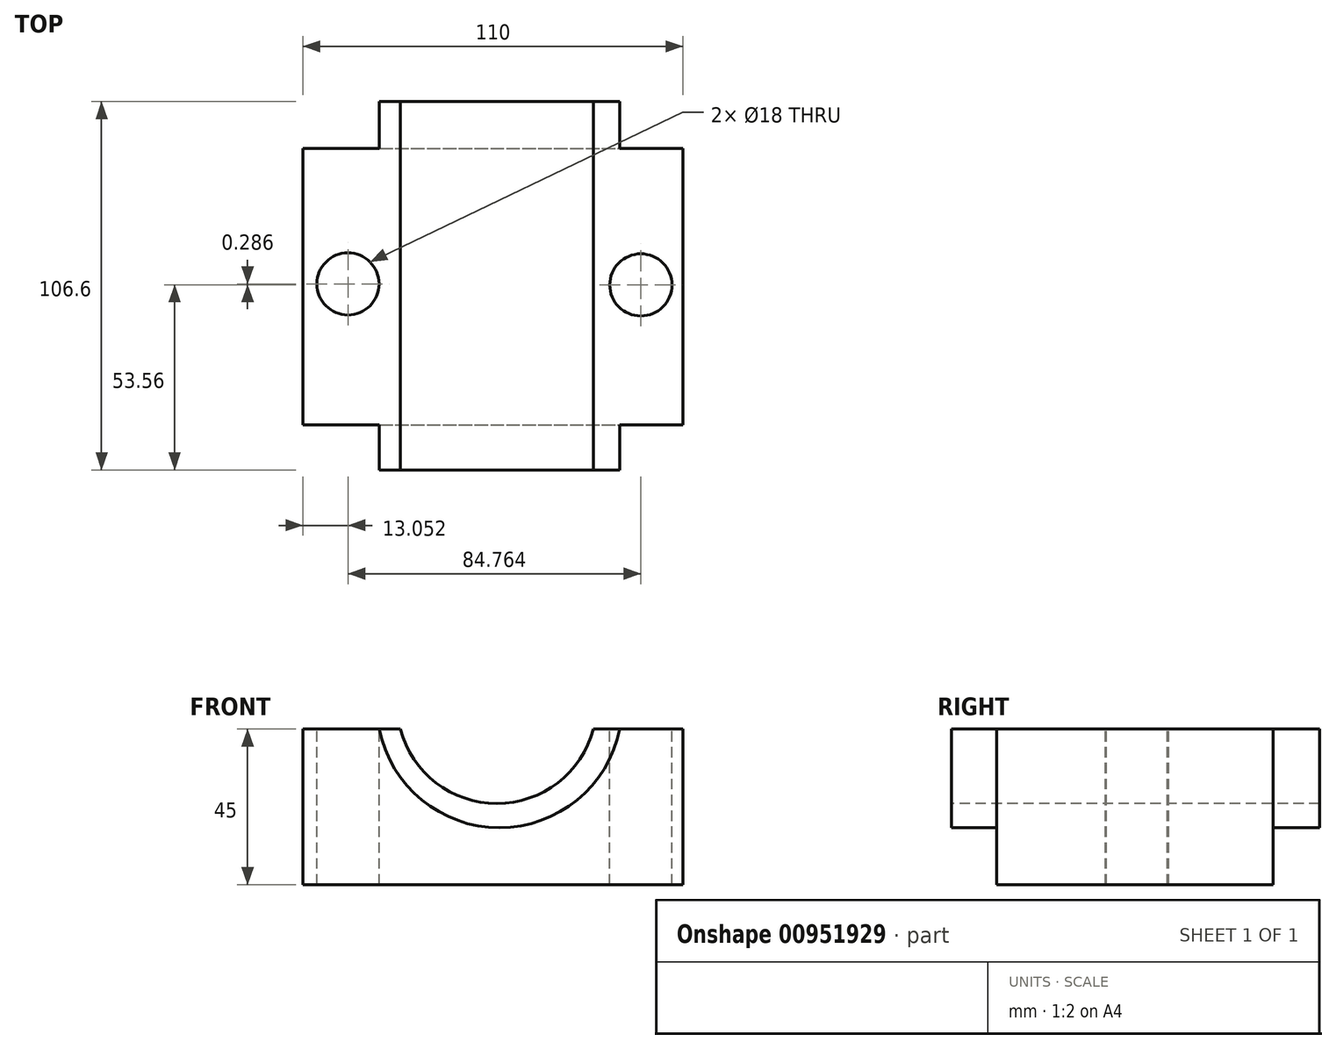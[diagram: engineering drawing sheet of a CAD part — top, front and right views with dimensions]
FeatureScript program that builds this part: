
annotation { "Feature Type Name" : "Feature", "Feature Type Description" : "" }
export const myFeature = defineFeature(function(context is Context, id is Id, definition is map)
    precondition{}
    {
        {
            var Q0;
            Q0=qCreatedBy(makeId("Top.planeOp"),FACE);
            var sketch = newSketch(context, id + "F0", { "sketchPlane" : qUnion([Q0])});
            skLineSegment(sketch, "E0.bottom", {"start": v(-46.7, 32.81) * mm, "end": v(63.3, 32.81) * mm});
            skLineSegment(sketch, "E0.top", {"start": v(-46.7, -47.19) * mm, "end": v(63.3, -47.19) * mm});
            skLineSegment(sketch, "E0.left", {"start": v(-46.7, 32.81) * mm, "end": v(-46.7, -47.19) * mm});
            skLineSegment(sketch, "E0.right", {"start": v(63.3, 32.81) * mm, "end": v(63.3, -47.19) * mm});
            skSolve(sketch);
        }
        {
            var Q0;
            Q0=makeQuery(id+"F0.imprint","IMPRINT",FACE,{"disambiguationData":[TD([[makeQuery(id+"F0.imprint","IMPRINT",EDGE,{"derivedFrom":sQuery(id+"F0.wireOp",EDGE,"E0.bottom")}),-1.0]])]});
            extrude(context, id + "F1", {"entities" : qUnion([Q0]), "oppositeDirection" : true, "depth" : 45 * mm, "offsetDistance" : 25 * mm});
        }
        {
            var Q0;
            Q0=makeQuery(id+"F1.opExtrude","SWEPT_FACE",FACE,{"disambiguationData":[OSD([sQuery(id+"F0.wireOp",EDGE,"E0.top")])]});
            var sketch = newSketch(context, id + "F2", { "sketchPlane" : qUnion([Q0])});
            skArc(sketch, "E1", {"start": v(-18.47, 0) * mm, "mid": v(9.45, -21.54) * mm, "end": v(37.37, 0) * mm});
            skSolve(sketch);
        }
        {
            var Q0;
            {var subQ0=sQuery(id+"F2.wireOp",EDGE,"E1");Q0=makeQuery(id+"F2.imprint","IMPRINT",FACE,{"disambiguationData":[TD([[makeQuery(id+"F2.imprint","IMPRINT",EDGE,{"derivedFrom":subQ0}),1.0]])]});}
            extrude(context, id + "F3", {"entities" : qUnion([Q0]), "operationType" : NewBodyOperationType.REMOVE, "oppositeDirection" : true, "depth" : 136.2 * mm, "offsetDistance" : 25 * mm});
        }
        {
            var Q0;
            Q0=makeQuery(id+"F1.opExtrude","SWEPT_FACE",FACE,{"disambiguationData":[OSD([sQuery(id+"F0.wireOp",EDGE,"E0.top")])]});
            var sketch = newSketch(context, id + "F4", { "sketchPlane" : qUnion([Q0])});
            skArc(sketch, "E2", {"start": v(-24.6, 0) * mm, "mid": v(10.2, -28.55) * mm, "end": v(45, 0) * mm});
            skSolve(sketch);
        }
        {
            var Q0;
            {var subQ0=sQuery(id+"F4.wireOp",EDGE,"E2");Q0=makeQuery(id+"F4.imprint","IMPRINT",FACE,{"disambiguationData":[TD([[makeQuery(id+"F4.imprint","IMPRINT",EDGE,{"derivedFrom":subQ0}),1.0]])]});}
            extrude(context, id + "F5", {"entities" : qUnion([Q0]), "operationType" : NewBodyOperationType.ADD, "oppositeDirection" : true, "depth" : 187 * mm, "offsetDistance" : 25 * mm, "symmetric" : true});
        }
        {
            var Q0;
            Q0=makeQuery(id+"F5.opExtrude","CAP_FACE",FACE,{"disambiguationData":[OSD([sQuery(id+"F0.wireOp",EDGE,"E0.top"),sQuery(id+"F2.wireOp",EDGE,"E1"),sQuery(id+"F4.wireOp",EDGE,"E2")])],"isStart":true});
            extrude(context, id + "F6", {"entities" : qUnion([Q0]), "operationType" : NewBodyOperationType.REMOVE, "oppositeDirection" : true, "depth" : 80.4 * mm, "offsetDistance" : 25 * mm});
        }
        {
            var Q0;
            {var subQ0=sQuery(id+"F0.wireOp",EDGE,"E0.left");var subQ1=sQuery(id+"F0.wireOp",EDGE,"E0.top");var subQ2=sQuery(id+"F0.wireOp",EDGE,"E0.bottom");var subQ3=makeQuery(id+"F1.opExtrude","CAP_FACE",FACE,{"disambiguationData":[OSD([subQ2,subQ1,subQ0,sQuery(id+"F0.wireOp",EDGE,"E0.right")])],"isStart":true});var subQ5=sQuery(id+"F2.wireOp",EDGE,"E1");var subQ7=makeQuery(id+"F1.opExtrude","SWEPT_FACE",FACE,{"disambiguationData":[OSD([subQ0])]});var subQ8=makeQuery(id+"F3.boolean.opBoolean","SPLIT",EDGE,{"disambiguationData":[TD([subQ7])],"derivedFrom":makeQuery(id+"F1.opExtrude","CAP_EDGE",EDGE,{"disambiguationData":[OSD([subQ1])],"isStart":true})});Q0=makeQuery(id+"F5.boolean.opBoolean","MERGE",FACE,{"derivedFrom":[makeQuery(id+"F3.boolean.opBoolean","SPLIT",FACE,{"disambiguationData":[TD([subQ7])],"derivedFrom":subQ3}),makeQuery(id+"F5.opExtrude","SWEPT_FACE",FACE,{"disambiguationData":[OSD([subQ1]),TDD([makeQuery(id+"F4.imprint","IMPRINT",EDGE,{"disambiguationData":[TD([[makeQuery(id+"F4.imprint","INTERSECT",VERTEX,{"derivedFrom":[makeQuery(id+"F3.boolean.opBoolean","COPY",EDGE,{"derivedFrom":makeQuery(id+"F3.opExtrude","CAP_EDGE",EDGE,{"disambiguationData":[OSD([subQ5])],"isStart":true})}),subQ8]}),1.0]])],"derivedFrom":subQ8})])]})]});}
            var sketch = newSketch(context, id + "F7", { "sketchPlane" : qUnion([Q0])});
            skCircle(sketch, "E3", {"center": v(-33.65, -6.44) * mm, "radius": 9 * mm});
            skSolve(sketch);
        }
        {
            var Q0;
            Q0=makeQuery(id+"F7.imprint","IMPRINT",FACE,{"disambiguationData":[TD([[makeQuery(id+"F7.imprint","IMPRINT",EDGE,{"derivedFrom":sQuery(id+"F7.wireOp",EDGE,"E3")}),1.0]])]});
            extrude(context, id + "F8", {"entities" : qUnion([Q0]), "operationType" : NewBodyOperationType.REMOVE, "oppositeDirection" : true, "depth" : 68 * mm, "offsetDistance" : 25 * mm});
        }
        {
            var Q0;
            {var subQ0=sQuery(id+"F0.wireOp",EDGE,"E0.right");var subQ1=sQuery(id+"F0.wireOp",EDGE,"E0.top");var subQ2=sQuery(id+"F0.wireOp",EDGE,"E0.bottom");var subQ3=makeQuery(id+"F1.opExtrude","CAP_FACE",FACE,{"disambiguationData":[OSD([subQ2,subQ1,sQuery(id+"F0.wireOp",EDGE,"E0.left"),subQ0])],"isStart":true});var subQ5=sQuery(id+"F2.wireOp",EDGE,"E1");var subQ7=makeQuery(id+"F1.opExtrude","SWEPT_FACE",FACE,{"disambiguationData":[OSD([subQ0])]});var subQ8=makeQuery(id+"F3.boolean.opBoolean","SPLIT",EDGE,{"disambiguationData":[TD([subQ7])],"derivedFrom":makeQuery(id+"F1.opExtrude","CAP_EDGE",EDGE,{"disambiguationData":[OSD([subQ1])],"isStart":true})});Q0=makeQuery(id+"F5.boolean.opBoolean","MERGE",FACE,{"derivedFrom":[makeQuery(id+"F3.boolean.opBoolean","SPLIT",FACE,{"disambiguationData":[TD([subQ7])],"derivedFrom":subQ3}),makeQuery(id+"F5.opExtrude","SWEPT_FACE",FACE,{"disambiguationData":[OSD([subQ1]),TDD([makeQuery(id+"F4.imprint","IMPRINT",EDGE,{"disambiguationData":[TD([[makeQuery(id+"F4.imprint","INTERSECT",VERTEX,{"derivedFrom":[makeQuery(id+"F3.boolean.opBoolean","COPY",EDGE,{"derivedFrom":makeQuery(id+"F3.opExtrude","CAP_EDGE",EDGE,{"disambiguationData":[OSD([subQ5])],"isStart":true})}),subQ8]}),-1.0]])],"derivedFrom":subQ8})])]})]});}
            var sketch = newSketch(context, id + "F9", { "sketchPlane" : qUnion([Q0])});
            skCircle(sketch, "E4", {"center": v(51.12, -6.73) * mm, "radius": 9 * mm});
            skSolve(sketch);
        }
        {
            var Q0;
            Q0=makeQuery(id+"F9.imprint","IMPRINT",FACE,{"disambiguationData":[TD([[makeQuery(id+"F9.imprint","IMPRINT",EDGE,{"derivedFrom":sQuery(id+"F9.wireOp",EDGE,"E4")}),1.0]])]});
            extrude(context, id + "F10", {"entities" : qUnion([Q0]), "operationType" : NewBodyOperationType.REMOVE, "oppositeDirection" : true, "depth" : 68.7 * mm, "offsetDistance" : 25 * mm});
        }
    });
